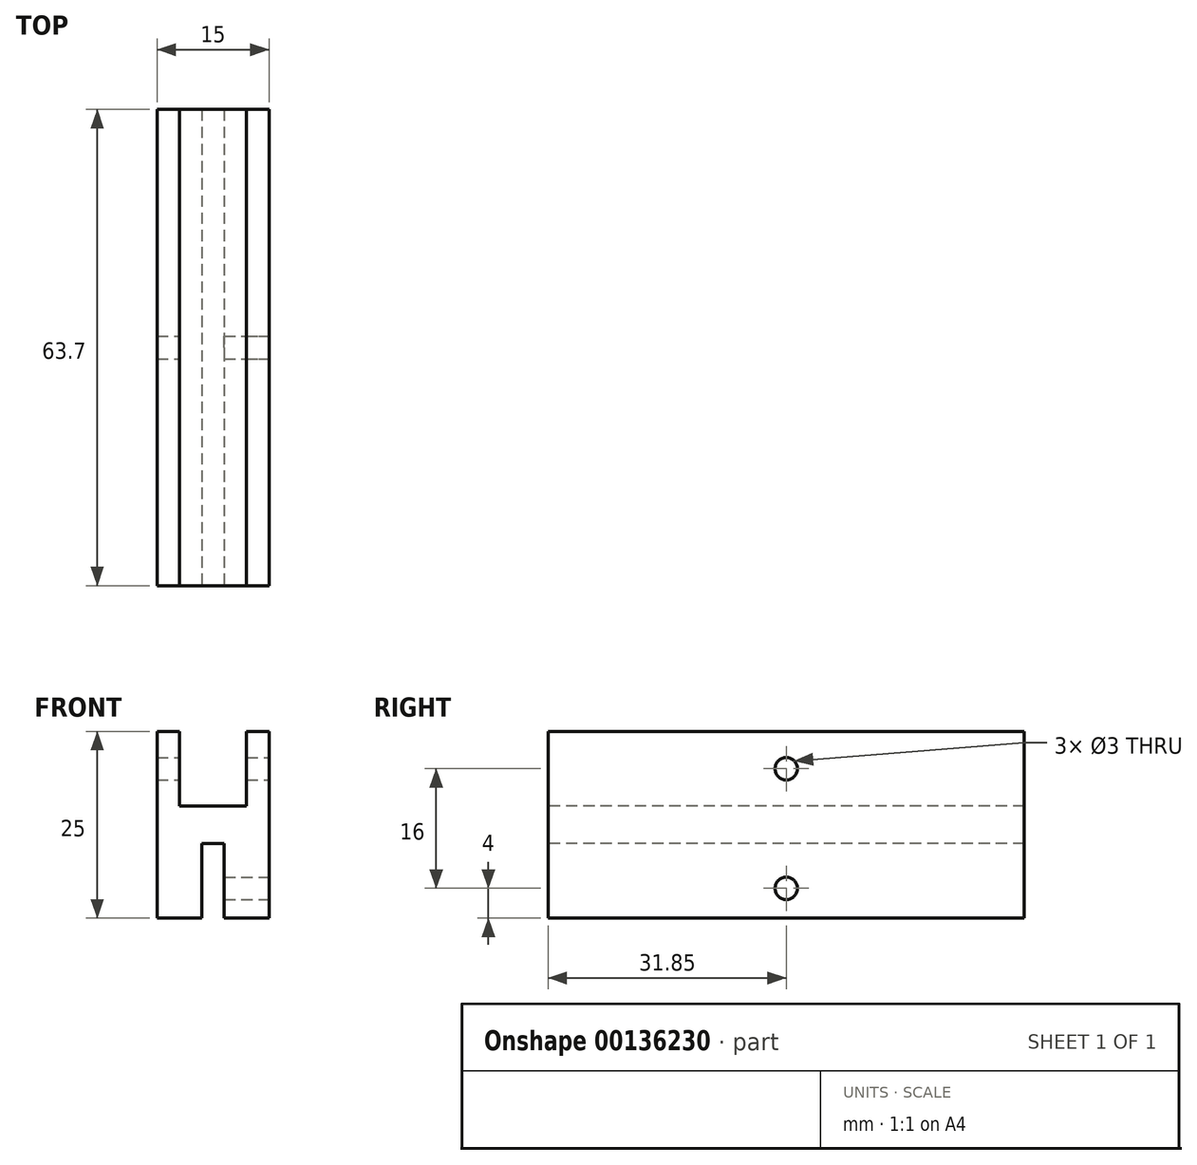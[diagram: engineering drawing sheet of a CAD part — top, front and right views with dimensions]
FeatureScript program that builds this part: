
annotation { "Feature Type Name" : "Feature", "Feature Type Description" : "" }
export const myFeature = defineFeature(function(context is Context, id is Id, definition is map)
    precondition{}
    {
        {
            var Q0;
            Q0=qCreatedBy(makeId("Front.planeOp"),FACE);
            var sketch = newSketch(context, id + "F0", { "sketchPlane" : qUnion([Q0])});
            skLineSegment(sketch, "E0.left", {"start": v(0, 0) * mm, "end": v(0, 25) * mm});
            skLineSegment(sketch, "E0.right", {"start": v(15, 0) * mm, "end": v(15, 25) * mm});
            skLineSegment(sketch, "E1", {"start": v(0, 0) * mm, "end": v(6, 0) * mm});
            skLineSegment(sketch, "E2", {"start": v(6, 0) * mm, "end": v(6, 10) * mm});
            skLineSegment(sketch, "E3", {"start": v(6, 10) * mm, "end": v(9, 10) * mm});
            skLineSegment(sketch, "E4", {"start": v(9, 10) * mm, "end": v(9, 0) * mm});
            skLineSegment(sketch, "E5", {"start": v(9, 0) * mm, "end": v(15, 0) * mm});
            skLineSegment(sketch, "E6", {"start": v(0, 25) * mm, "end": v(3, 25) * mm});
            skLineSegment(sketch, "E7", {"start": v(3, 25) * mm, "end": v(3, 15) * mm});
            skLineSegment(sketch, "E8", {"start": v(3, 15) * mm, "end": v(12, 15) * mm});
            skLineSegment(sketch, "E9", {"start": v(12, 15) * mm, "end": v(12, 25) * mm});
            skLineSegment(sketch, "E10", {"start": v(12, 25) * mm, "end": v(15, 25) * mm});
            skSolve(sketch);
        }
        {
            var Q0;
            Q0 = qSketchRegion(id + "F0", true);
            extrude(context, id + "F1", {"entities" : qUnion([Q0]), "oppositeDirection" : true, "depth" : 63.7 * mm});
        }
        {
            var Q0;
            Q0=makeQuery(id+"F1.opExtrude","SWEPT_FACE",FACE,{"disambiguationData":[OSD([sQuery(id+"F0.wireOp",EDGE,"E0.right")])]});
            var sketch = newSketch(context, id + "F2", { "sketchPlane" : qUnion([Q0])});
            skCircle(sketch, "E11", {"center": v(31.85, 4) * mm, "radius": 1.5 * mm});
            skPoint(sketch, "E11.centerSnap0", {"position": v(31.85, 0) * mm});
            skCircle(sketch, "E12", {"center": v(31.85, 20) * mm, "radius": 1.5 * mm});
            skSolve(sketch);
        }
        {
            var Q0;
            Q0=makeQuery(id+"F2.imprint","IMPRINT",FACE,{"disambiguationData":[TD([[makeQuery(id+"F2.imprint","IMPRINT",EDGE,{"derivedFrom":sQuery(id+"F2.wireOp",EDGE,"E12")}),1.0]])]});
            extrude(context, id + "F3", {"entities" : qUnion([Q0]), "operationType" : NewBodyOperationType.REMOVE, "oppositeDirection" : true, "depth" : 25 * mm});
        }
        {
            var Q0;
            Q0=makeQuery(id+"F2.imprint","IMPRINT",FACE,{"disambiguationData":[TD([[makeQuery(id+"F2.imprint","IMPRINT",EDGE,{"derivedFrom":sQuery(id+"F2.wireOp",EDGE,"E11")}),1.0]])]});
            extrude(context, id + "F4", {"entities" : qUnion([Q0]), "operationType" : NewBodyOperationType.REMOVE, "oppositeDirection" : true, "depth" : 8 * mm});
        }
        {
            var Q0;
            Q0=makeQuery(id+"F1.opExtrude","CAP_FACE",FACE,{"disambiguationData":[OSD([sQuery(id+"F0.wireOp",EDGE,"E0.left"),sQuery(id+"F0.wireOp",EDGE,"E0.right"),sQuery(id+"F0.wireOp",EDGE,"E1"),sQuery(id+"F0.wireOp",EDGE,"E2"),sQuery(id+"F0.wireOp",EDGE,"E3"),sQuery(id+"F0.wireOp",EDGE,"E4"),sQuery(id+"F0.wireOp",EDGE,"E5"),sQuery(id+"F0.wireOp",EDGE,"E6"),sQuery(id+"F0.wireOp",EDGE,"E7"),sQuery(id+"F0.wireOp",EDGE,"E8"),sQuery(id+"F0.wireOp",EDGE,"E9"),sQuery(id+"F0.wireOp",EDGE,"E10")])],"isStart":true});
            var sketch = newSketch(context, id + "F5", { "sketchPlane" : qUnion([Q0])});
            skLineSegment(sketch, "E13", {"start": v(10, 0) * mm, "end": v(15, 12) * mm});
            skLineSegment(sketch, "E14", {"start": v(7.5, 28.6) * mm, "end": v(7.5, -5.3) * mm, "construction": true});
            skPoint(sketch, "E14.startSnap0", {"position": v(7.5, 10) * mm});
            skPoint(sketch, "E14.endSnap0", {"position": v(7.5, 10) * mm});
            skLineSegment(sketch, "E15.MirrorCS", {"start": v(5, 0) * mm, "end": v(0, 12) * mm});
            skLineSegment(sketch, "E16", {"start": v(15, 12) * mm, "end": v(15, 0) * mm});
            skLineSegment(sketch, "E17", {"start": v(15, 0) * mm, "end": v(10, 0) * mm});
            skLineSegment(sketch, "E18", {"start": v(5, 0) * mm, "end": v(0, 0) * mm});
            skLineSegment(sketch, "E19", {"start": v(0, 0) * mm, "end": v(0, 12) * mm});
            skSolve(sketch);
        }
    });
